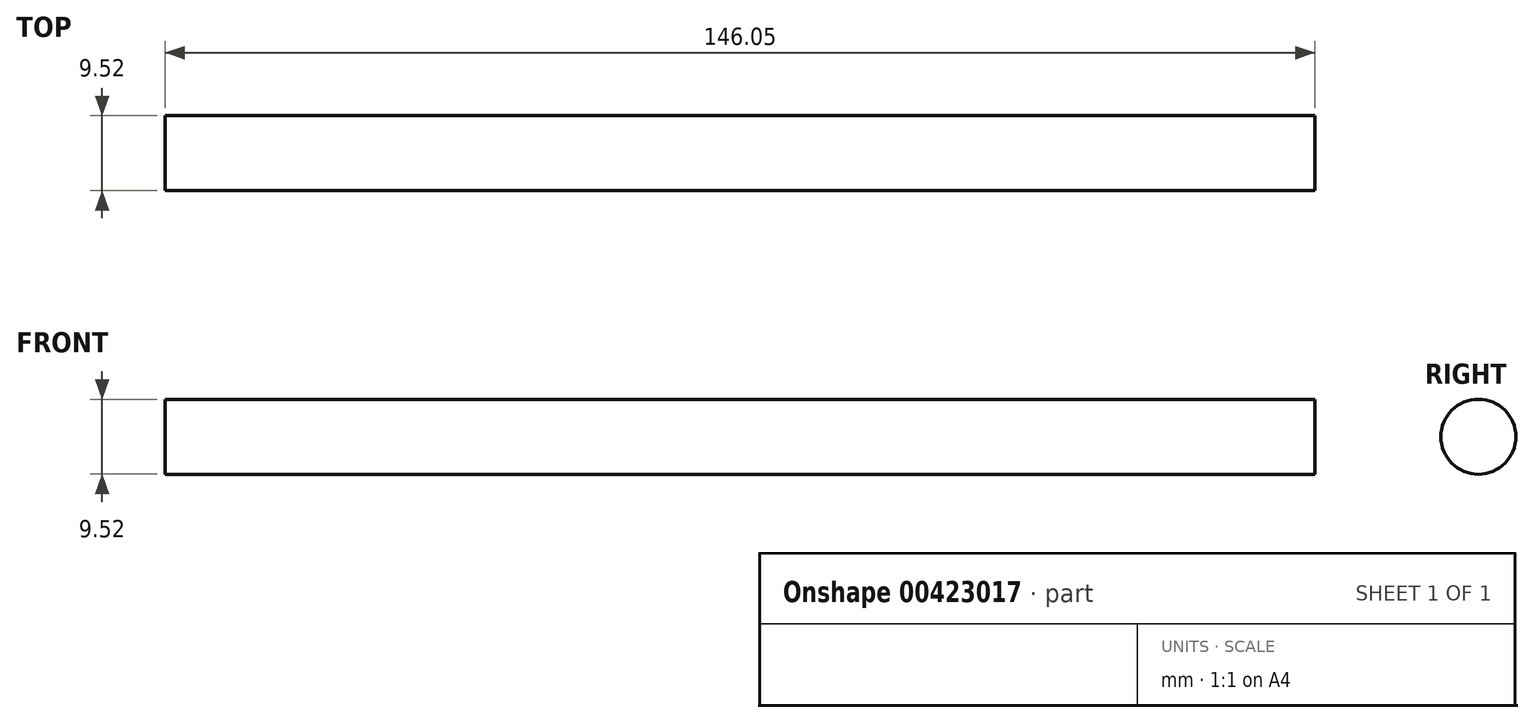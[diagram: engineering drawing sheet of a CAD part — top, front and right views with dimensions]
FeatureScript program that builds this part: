
annotation { "Feature Type Name" : "Feature", "Feature Type Description" : "" }
export const myFeature = defineFeature(function(context is Context, id is Id, definition is map)
    precondition{}
    {
        {
            var Q0;
            Q0=qCreatedBy(makeId("Right.planeOp"),FACE);
            var sketch = newSketch(context, id + "F0", { "sketchPlane" : qUnion([Q0])});
            skCircle(sketch, "E0", {"center": v(0, 0) * mm, "radius": 4.76 * mm});
            skSolve(sketch);
        }
        {
            var Q0;
            Q0=qSketchRegion(id+"F0",true);
            extrude(context, id + "F1", {"entities" : qUnion([Q0]), "depth" : 146.05 * mm});
        }
    });
